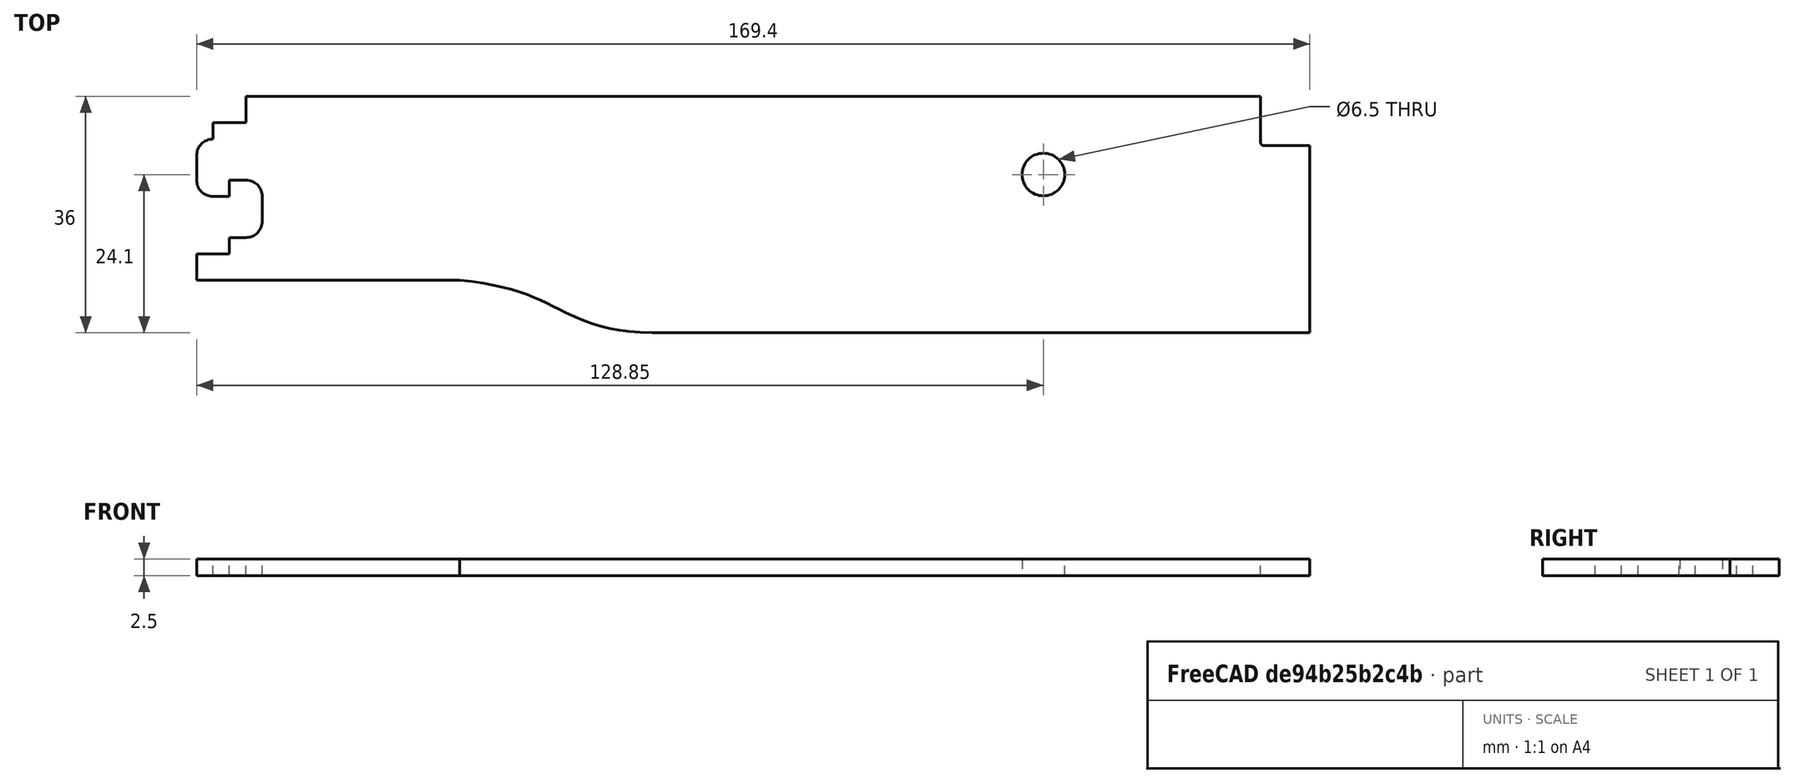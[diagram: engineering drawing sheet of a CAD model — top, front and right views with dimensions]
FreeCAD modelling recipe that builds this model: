
FCSTD DOCUMENT  (FreeCAD 0.19R0.19.2)
Label: v0_13
License: All rights reserved
LicenseURL: http://en.wikipedia.org/wiki/All_rights_reserved
objects: Sketcher::SketchObject×2, Part::Extrusion×1
note: 3 computed .brp shape members not serialized (recipe doc carries the construction recipe); baked Part::Feature solids carry a one-line shape summary decoded from their .brp

FEATURE [Sketcher::SketchObject] Sketch
  FullyConstrained = true
  sketch-geometry (33):
    g0: LineSegment StartX=0 StartY=0 StartZ=0 EndX=154.4 EndY=0 EndZ=0
    g1: LineSegment StartX=154.4 StartY=0 StartZ=0 EndX=154.4 EndY=-7 EndZ=0
    g2: LineSegment StartX=154.9 StartY=-7.5 StartZ=0 EndX=161.9 EndY=-7.5 EndZ=0
    g3: ArcOfCircle CenterX=154.9 CenterY=-7 CenterZ=0 NormalX=0 NormalY=0 NormalZ=1 AngleXU=0 Radius=0.5 StartAngle=3.14159 EndAngle=4.71239
    g4: Circle CenterX=121.35 CenterY=-11.9 CenterZ=0 NormalX=0 NormalY=0 NormalZ=1 AngleXU=0 Radius=3.25
    g5: LineSegment StartX=0 StartY=0 StartZ=0 EndX=0 EndY=-4 EndZ=0
    g6: LineSegment StartX=-5 StartY=-4 StartZ=0 EndX=0 EndY=-4 EndZ=0
    g7: LineSegment StartX=-5 StartY=-4 StartZ=0 EndX=-5 EndY=-6.5 EndZ=0
    g8: LineSegment StartX=-7.5 StartY=-9 StartZ=0 EndX=-7.5 EndY=-12.75 EndZ=0
    g9: ArcOfCircle CenterX=-5 CenterY=-9 CenterZ=0 NormalX=0 NormalY=0 NormalZ=1 AngleXU=0 Radius=2.5 StartAngle=1.5708 EndAngle=3.14159
    g10: LineSegment StartX=-5 StartY=-15.25 StartZ=0 EndX=-2.5 EndY=-15.25 EndZ=0
    g11: ArcOfCircle CenterX=-5 CenterY=-12.75 CenterZ=0 NormalX=0 NormalY=0 NormalZ=1 AngleXU=0 Radius=2.5 StartAngle=3.14159 EndAngle=4.71239
    g12: LineSegment StartX=-2.5 StartY=-15.25 StartZ=0 EndX=-2.5 EndY=-12.75 EndZ=0
    g13: LineSegment StartX=-2.5 StartY=-12.75 StartZ=0 EndX=1.488e-13 EndY=-12.75 EndZ=0
    g14: ArcOfCircle CenterX=1.486e-13 CenterY=-15.25 CenterZ=0 NormalX=0 NormalY=0 NormalZ=1 AngleXU=0 Radius=2.5 StartAngle=8e-16 EndAngle=1.5708
    g15: LineSegment StartX=2.5 StartY=-15.25 StartZ=0 EndX=2.5 EndY=-19 EndZ=0
    g16: ArcOfCircle CenterX=1.483e-13 CenterY=-19 CenterZ=0 NormalX=0 NormalY=0 NormalZ=1 AngleXU=0 Radius=2.5 StartAngle=4.71239 EndAngle=6.28319
    g17: LineSegment StartX=-2.5 StartY=-21.5 StartZ=0 EndX=1.479e-13 EndY=-21.5 EndZ=0
    g18: LineSegment StartX=-2.5 StartY=-21.5 StartZ=0 EndX=-2.5 EndY=-24 EndZ=0
    g19: LineSegment StartX=-7.5 StartY=-24 StartZ=0 EndX=-2.5 EndY=-24 EndZ=0
    g20: LineSegment StartX=-7.5 StartY=-24 StartZ=0 EndX=-7.5 EndY=-28 EndZ=0
    g21: LineSegment StartX=161.9 StartY=-7.5 StartZ=0 EndX=161.9 EndY=-36 EndZ=0
    g22: LineSegment StartX=61.85 StartY=-36 StartZ=0 EndX=161.9 EndY=-36 EndZ=0
    g23-g27: Circle x5 (B-spline internal-alignment scaffolding for g28; pole/knot coordinates omitted)
    g28: BSplineCurve PolesCount=5 KnotsCount=3 Degree=3 IsPeriodic=0
    g29: GeomPoint X=61.85 Y=-36 Z=0
    g30: GeomPoint X=47.2264 Y=-32.2128 Z=0
    g31: GeomPoint X=32.5209 Y=-28 Z=0
    g32: LineSegment StartX=32.5209 StartY=-28 StartZ=0 EndX=-7.5 EndY=-28 EndZ=0
  constraints (75):
    c: PointOnObject(g0,g-2)
    c: Horizontal(g0)
    c: Distance(g0) = 154.4
    c: DistanceY(g-1,g0) = 0
    c: Vertical(g1)
    c: Distance(g1) = 7
    c: Coincident(g1,g0)
    c: Horizontal(g2)
    c: Distance(g2) = 7
    c: Coincident(g3,g1)
    c: Tangent(g2,g3)
    c: Tangent(g2,g3,g2) = -1.5708
    c: Block(g3)
    c: Block(g4)
    c: Vertical(g5)
    c: Distance(g5) = 4
    c: Coincident(g5,g0)
    c: Horizontal(g6)
    c: Distance(g6) = 5
    c: Coincident(g6,g5)
    c: Vertical(g7)
    c: Distance(g7) = 2.5
    c: Coincident(g7,g6)
    c: Vertical(g8)
    c: Distance(g8) = 3.75
    c: Coincident(g9,g7)
    c: Block(g9)
    c: Coincident(g8,g9)
    c: Horizontal(g10)
    c: Distance(g10) = 2.5
    c: Coincident(g11,g8)
    c: Block(g11)
    c: Block(g10)
    c: Vertical(g12)
    c: Distance(g12) = 2.5
    c: Coincident(g12,g10)
    c: Horizontal(g13)
    c: Distance(g13) = 2.5
    c: Coincident(g13,g12)
    c: Coincident(g14,g13)
    c: Vertical(g15)
    c: Distance(g15) = 3.75
    c: Block(g14)
    c: Coincident(g15,g14)
    c: Coincident(g16,g15)
    c: Block(g16)
    c: Horizontal(g17)
    c: Distance(g17) = 2.5
    c: Coincident(g17,g16)
    c: Vertical(g18)
    c: Distance(g18) = 2.5
    c: Coincident(g18,g17)
    c: Horizontal(g19)
    c: Distance(g19) = 5
    c: Coincident(g19,g18)
    c: Vertical(g20)
    c: Distance(g20) = 4
    c: Coincident(g20,g19)
    c: Vertical(g21)
    c: Distance(g21) = 28.5
    c: Coincident(g21,g2)
    c: Horizontal(g22)
    c: Distance(g22) = 100.05
    c: Coincident(g22,g21)
    c: Coincident(g28,g22)
    c: Weight(g23) = 1
    c: Equal(g23, g24-g27) x4
    c: InternalAlignment(g23-g27 -> g28) x5
    c: InternalAlignment(g29,g28)
    c: InternalAlignment(g30,g28)
    c: InternalAlignment(g31,g28)
    c: Horizontal(g32)
    c: Coincident(g32,g20)
    c: Coincident(g32,g28)
    c: Block(g28)
FEATURE [Part::Extrusion] Extrude
  Base = -> Sketch
  Dir = (0,0,1)
  DirMode = 2
  FaceMakerClass = Part::FaceMakerBullseye
  LengthFwd = 2.5
  LengthRev = 0
  Solid = true
  Symmetric = false
FEATURE [Sketcher::SketchObject] Sketch001
  FullyConstrained = true
  sketch-geometry (36):
    g0: LineSegment StartX=0 StartY=0 StartZ=0 EndX=154.4 EndY=0 EndZ=0
    g1: LineSegment StartX=154.4 StartY=0 StartZ=0 EndX=154.4 EndY=-7 EndZ=0
    g2: LineSegment StartX=154.9 StartY=-7.5 StartZ=0 EndX=161.9 EndY=-7.5 EndZ=0
    g3: ArcOfCircle CenterX=154.9 CenterY=-7 CenterZ=0 NormalX=0 NormalY=0 NormalZ=1 AngleXU=0 Radius=0.5 StartAngle=3.14159 EndAngle=4.71239
    g4: Circle CenterX=121.35 CenterY=-11.9 CenterZ=0 NormalX=0 NormalY=0 NormalZ=1 AngleXU=0 Radius=3.25
    g5: LineSegment StartX=0 StartY=0 StartZ=0 EndX=0 EndY=-4 EndZ=0
    g6: LineSegment StartX=-5 StartY=-4 StartZ=0 EndX=0 EndY=-4 EndZ=0
    g7: LineSegment StartX=-5 StartY=-4 StartZ=0 EndX=-5 EndY=-6.5 EndZ=0
    g8: LineSegment StartX=-7.5 StartY=-9 StartZ=0 EndX=-7.5 EndY=-12.75 EndZ=0
    g9: ArcOfCircle CenterX=-5 CenterY=-9 CenterZ=0 NormalX=0 NormalY=0 NormalZ=1 AngleXU=0 Radius=2.5 StartAngle=1.5708 EndAngle=3.14159
    g10: LineSegment StartX=-5 StartY=-15.25 StartZ=0 EndX=-2.5 EndY=-15.25 EndZ=0
    g11: ArcOfCircle CenterX=-5 CenterY=-12.75 CenterZ=0 NormalX=0 NormalY=0 NormalZ=1 AngleXU=0 Radius=2.5 StartAngle=3.14159 EndAngle=4.71239
    g12: LineSegment StartX=-2.5 StartY=-15.25 StartZ=0 EndX=-2.5 EndY=-12.75 EndZ=0
    g13: LineSegment StartX=-2.5 StartY=-12.75 StartZ=0 EndX=1.488e-13 EndY=-12.75 EndZ=0
    g14: ArcOfCircle CenterX=1.486e-13 CenterY=-15.25 CenterZ=0 NormalX=0 NormalY=0 NormalZ=1 AngleXU=0 Radius=2.5 StartAngle=8e-16 EndAngle=1.5708
    g15: LineSegment StartX=2.5 StartY=-15.25 StartZ=0 EndX=2.5 EndY=-19 EndZ=0
    g16: ArcOfCircle CenterX=1.483e-13 CenterY=-19 CenterZ=0 NormalX=0 NormalY=0 NormalZ=1 AngleXU=0 Radius=2.5 StartAngle=4.71239 EndAngle=6.28319
    g17: LineSegment StartX=-2.5 StartY=-21.5 StartZ=0 EndX=1.479e-13 EndY=-21.5 EndZ=0
    g18: LineSegment StartX=-2.5 StartY=-21.5 StartZ=0 EndX=-2.5 EndY=-24 EndZ=0
    g19: LineSegment StartX=-7.5 StartY=-24 StartZ=0 EndX=-2.5 EndY=-24 EndZ=0
    g20: LineSegment StartX=-7.5 StartY=-24 StartZ=0 EndX=-7.5 EndY=-28 EndZ=0
    g21: LineSegment StartX=161.9 StartY=-7.5 StartZ=0 EndX=161.9 EndY=-36 EndZ=0
    g22: LineSegment StartX=61.85 StartY=-36 StartZ=0 EndX=161.9 EndY=-36 EndZ=0
    g23-g27: Circle x5 (B-spline internal-alignment scaffolding for g28; pole/knot coordinates omitted)
    g28: BSplineCurve PolesCount=5 KnotsCount=3 Degree=3 IsPeriodic=0
    g29: GeomPoint X=61.85 Y=-36 Z=0
    g30: GeomPoint X=47.2264 Y=-32.2128 Z=0
    g31: GeomPoint X=32.5209 Y=-28 Z=0
    g32: LineSegment StartX=32.5209 StartY=-28 StartZ=0 EndX=-7.5 EndY=-28 EndZ=0
    g33: LineSegment StartX=154.4 StartY=-5 StartZ=0 EndX=121.35 EndY=-5 EndZ=0
    g34: LineSegment StartX=154.4 StartY=-5 StartZ=0 EndX=149.4 EndY=-5 EndZ=0
    g35: LineSegment StartX=149.4 StartY=-36 StartZ=0 EndX=149.4 EndY=-31 EndZ=0
  constraints (83):
    c: PointOnObject(g0,g-2)
    c: Horizontal(g0)
    c: Distance(g0) = 154.4
    c: DistanceY(g-1,g0) = 0
    c: Vertical(g1)
    c: Distance(g1) = 7
    c: Coincident(g1,g0)
    c: Horizontal(g2)
    c: Distance(g2) = 7
    c: Coincident(g3,g1)
    c: Tangent(g2,g3)
    c: Tangent(g2,g3,g2) = -1.5708
    c: Block(g3)
    c: Block(g4)
    c: Vertical(g5)
    c: Distance(g5) = 4
    c: Coincident(g5,g0)
    c: Horizontal(g6)
    c: Distance(g6) = 5
    c: Coincident(g6,g5)
    c: Vertical(g7)
    c: Distance(g7) = 2.5
    c: Coincident(g7,g6)
    c: Vertical(g8)
    c: Distance(g8) = 3.75
    c: Coincident(g9,g7)
    c: Block(g9)
    c: Coincident(g8,g9)
    c: Horizontal(g10)
    c: Distance(g10) = 2.5
    c: Coincident(g11,g8)
    c: Block(g11)
    c: Block(g10)
    c: Vertical(g12)
    c: Distance(g12) = 2.5
    c: Coincident(g12,g10)
    c: Horizontal(g13)
    c: Distance(g13) = 2.5
    c: Coincident(g13,g12)
    c: Coincident(g14,g13)
    c: Vertical(g15)
    c: Distance(g15) = 3.75
    c: Block(g14)
    c: Coincident(g15,g14)
    c: Coincident(g16,g15)
    c: Block(g16)
    c: Horizontal(g17)
    c: Distance(g17) = 2.5
    c: Coincident(g17,g16)
    c: Vertical(g18)
    c: Distance(g18) = 2.5
    c: Coincident(g18,g17)
    c: Horizontal(g19)
    c: Distance(g19) = 5
    c: Coincident(g19,g18)
    c: Vertical(g20)
    c: Distance(g20) = 4
    c: Coincident(g20,g19)
    c: Vertical(g21)
    c: Distance(g21) = 28.5
    c: Coincident(g21,g2)
    c: Horizontal(g22)
    c: Distance(g22) = 100.05
    c: Coincident(g22,g21)
    c: Coincident(g28,g22)
    c: Weight(g23) = 1
    c: Equal(g23, g24-g27) x4
    c: InternalAlignment(g23-g27 -> g28) x5
    c: InternalAlignment(g29,g28)
    c: InternalAlignment(g30,g28)
    c: InternalAlignment(g31,g28)
    c: Horizontal(g32)
    c: Coincident(g32,g20)
    c: Coincident(g32,g28)
    c: Block(g28)
    c: Horizontal(g33)
    c: Horizontal(g34)
    c: Distance(g34) = 5
    c: Block(g33)
    c: Coincident(g34,g33)
    c: Vertical(g35)
    c: Distance(g35) = 5
    c: Block(g35)
